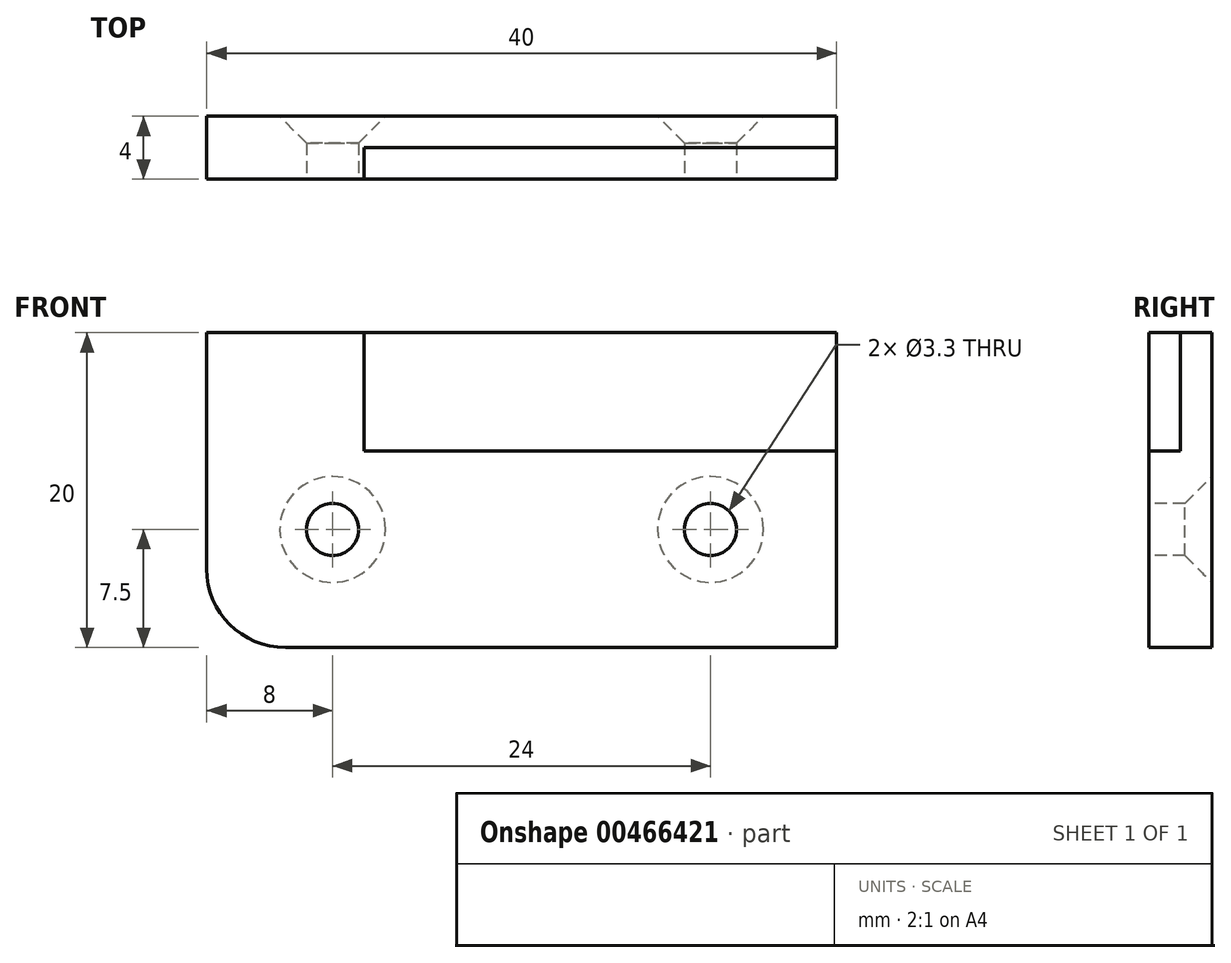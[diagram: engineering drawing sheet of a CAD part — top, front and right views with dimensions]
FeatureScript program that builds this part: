
annotation { "Feature Type Name" : "Feature", "Feature Type Description" : "" }
export const myFeature = defineFeature(function(context is Context, id is Id, definition is map)
    precondition{}
    {
        {
            var Q0;
            Q0=qCreatedBy(makeId("Front.planeOp"),FACE);
            var sketch = newSketch(context, id + "F0", { "sketchPlane" : qUnion([Q0])});
            skLineSegment(sketch, "E0.bottom", {"start": v(20, -10) * mm, "end": v(-20, -10) * mm});
            skLineSegment(sketch, "E0.top", {"start": v(20, 10) * mm, "end": v(-20, 10) * mm});
            skLineSegment(sketch, "E0.left", {"start": v(20, -10) * mm, "end": v(20, 10) * mm});
            skLineSegment(sketch, "E0.right", {"start": v(-20, -10) * mm, "end": v(-20, 10) * mm});
            skPoint(sketch, "E0.middle", {"position": v(0, 0) * mm});
            skPoint(sketch, "E1.startSnap0", {"position": v(-20, 0) * mm});
            skLineSegment(sketch, "E2", {"start": v(-20, 2.5) * mm, "end": v(20, 2.5) * mm});
            skPoint(sketch, "E3", {"position": v(-12, -2.5) * mm});
            skPoint(sketch, "E4", {"position": v(12, -2.5) * mm});
            skLineSegment(sketch, "E5", {"start": v(-20, -2.5) * mm, "end": v(20, -2.5) * mm, "construction": true});
            skLineSegment(sketch, "E6", {"start": v(-10, 10) * mm, "end": v(-10, 2.5) * mm});
            skSolve(sketch);
        }
        {
            var Q0;
            {var subQ3=sQuery(id+"F0.wireOp",EDGE,"E6");Q0=makeQuery(id+"F0.imprint","IMPRINT",FACE,{"disambiguationData":[TD([[makeQuery(id+"F0.imprint","IMPRINT",EDGE,{"derivedFrom":subQ3}),1.0]])]});}
            extrude(context, id + "F1", {"entities" : qUnion([Q0]), "depth" : 2 * mm, "offsetDistance" : 25 * mm});
        }
        {
            var Q0;
            {var subQ0=sQuery(id+"F0.wireOp",EDGE,"E0.bottom");Q0=makeQuery(id+"F0.imprint","IMPRINT",FACE,{"disambiguationData":[TD([[makeQuery(id+"F0.imprint","IMPRINT",EDGE,{"derivedFrom":subQ0}),-1.0]])]});}
            var Q1;
            {var subQ3=sQuery(id+"F0.wireOp",EDGE,"E6");Q1=makeQuery(id+"F0.imprint","IMPRINT",FACE,{"disambiguationData":[TD([[makeQuery(id+"F0.imprint","IMPRINT",EDGE,{"derivedFrom":subQ3}),-1.0]])]});}
            extrude(context, id + "F2", {"entities" : qUnion([Q0, Q1]), "operationType" : NewBodyOperationType.ADD, "depth" : 4 * mm, "offsetDistance" : 25 * mm});
        }
        {
            var Q0;
            Q0=sQuery(id+"F0.wireOp",VERTEX,"E3");
            var Q1;
            Q1=sQuery(id+"F0.wireOp",VERTEX,"E4");
            var Q2;
            Q2=makeQuery(id+"F1.opExtrude","SWEPT_BODY",BODY,{"disambiguationData":[OSD([sQuery(id+"F0.wireOp",EDGE,"E0.top"),sQuery(id+"F0.wireOp",EDGE,"E0.left"),sQuery(id+"F0.wireOp",EDGE,"E0.right"),sQuery(id+"F0.wireOp",EDGE,"E2")])]});
            hole(context, id + "F3", {"style" : HoleStyle.C_SINK, "endStyle" : HoleEndStyle.THROUGH, "oppositeDirection" : true, "standardTappedOrClearance" : lookupTablePath({ "standard" : "ISO", "fit" : "Normal", "size" : "M3", "type" : "Clearance" }), "standardBlindInLast" : lookupTablePath({ "fit" : "Standard", "standard" : "ISO", "size" : "M3", "type" : "Clearance" }), "holeDiameter" : 3.3 * mm, "cSinkDiameter" : 6.72 * mm, "cSinkAngle" : 90 * degree, "majorDiameter" : 5 * mm, "isTappedThrough" : true, "tappedDepth" : 12 * mm, "tapClearance" : 3, "locations" : qUnion([Q0, Q1]), "scope" : qUnion([Q2]), "startStyle" : HoleStartStyle.PART});
        }
        {
            var Q0;
            Q0=makeQuery(id+"F2.opExtrude","SWEPT_EDGE",EDGE,{"disambiguationData":[OSD([sQuery(id+"F0.wireOp",EDGE,"E0.bottom"),sQuery(id+"F0.wireOp",EDGE,"E0.right")])]});
            fillet(context, id + "F4", {"entities" : qUnion([Q0]), "radius" : 5 * mm, "tangentPropagation" : true, "allowEdgeOverflow" : false});
        }
    });
